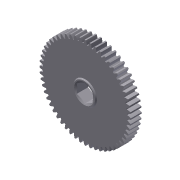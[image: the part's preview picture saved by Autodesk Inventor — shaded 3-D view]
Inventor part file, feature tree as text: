
AUTODESK INVENTOR PART (.ipt)
format: ipt  version: 2013 (Build 170138000, 138)  size: 410,112 bytes
history: native  units: mm (DEFAULTED — no unit token found)
features: sketch x5, extrude x3, plane x3, other x3, revolve x1, projected_geometry x1
ambient origin geometry x8: Origin, YZ Plane, XZ Plane, XY Plane, X Axis, Y Axis, Z Axis, Center Point
bodies: Solid1 (feature_tree)
feature tree (16):
  extrude  "Extrusion1"  Depth=8.7376mm TaperAngle=0.0deg
  plane  "Work Plane1"
  plane  "Work Plane2"
  plane  "Work Plane3"
  other  "Spur Gear"
  extrude  "Extrusion2"  Depth=76.2mm TaperAngle=0.0deg
  extrude  "Extrusion3"  Depth=19.05mm
  revolve  "Revolution1"  [1 undecoded]
  sketch  "Sketch1"  dims[d0=73.66mm d1=8.7376mm d2=0.0mm]
  sketch  "Sketch2"  dims[d3=71.12mm d4=76.2mm d5=0.0mm]
  other  "Srf1"
  sketch  "Sketch3"  dims[d6=0.0mm d7=0.560999mm d20=19.05mm]
  sketch  "Sketch4"  dims[d21=0.9144mm d22=0.0mm d23=12.7mm]
  sketch  "Sketch5"  dims[d24=0.635mm d25=0.0mm d27=0.889mm d28=0.635mm d29=5.070181mm d30=2.54mm d31=90.0deg]
  other  "Pitch Diameter"
  projected_geometry  "Project Cut Edges1"
note: 1 required parameter value undecoded (feature->parameter linkage not recoverable at this tier; creation-order binding heuristic only, values carry confidence <= 0.55)
